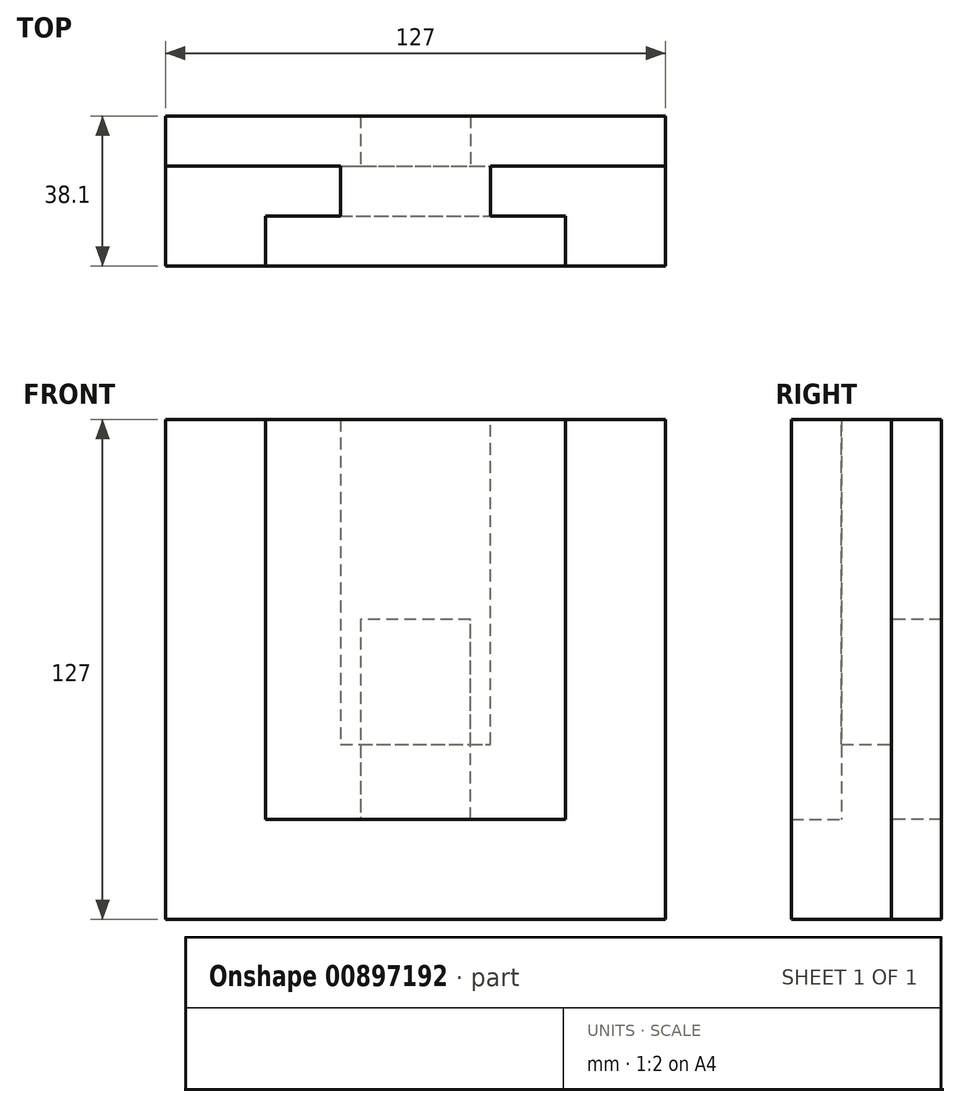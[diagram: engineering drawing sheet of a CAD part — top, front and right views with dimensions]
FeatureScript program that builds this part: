
annotation { "Feature Type Name" : "Feature", "Feature Type Description" : "" }
export const myFeature = defineFeature(function(context is Context, id is Id, definition is map)
    precondition{}
    {
        {
            var Q0;
            Q0=qCreatedBy(makeId("Front.planeOp"),FACE);
            var sketch = newSketch(context, id + "F0", { "sketchPlane" : qUnion([Q0])});
            skLineSegment(sketch, "E0.bottom", {"start": v(-63.5, 63.5) * mm, "end": v(63.5, 63.5) * mm});
            skLineSegment(sketch, "E0.top", {"start": v(-63.5, -63.5) * mm, "end": v(63.5, -63.5) * mm});
            skLineSegment(sketch, "E0.left", {"start": v(-63.5, 63.5) * mm, "end": v(-63.5, -63.5) * mm});
            skLineSegment(sketch, "E0.right", {"start": v(63.5, 63.5) * mm, "end": v(63.5, -63.5) * mm});
            skPoint(sketch, "E0.middle", {"position": v(0, 0) * mm});
            skLineSegment(sketch, "E1", {"start": v(-38.1, 63.5) * mm, "end": v(-38.1, -38.1) * mm});
            skLineSegment(sketch, "E2", {"start": v(-38.1, -38.1) * mm, "end": v(38.1, -38.1) * mm});
            skLineSegment(sketch, "E3", {"start": v(38.1, -38.1) * mm, "end": v(38.1, 63.5) * mm});
            skLineSegment(sketch, "E4", {"start": v(-19.05, 63.5) * mm, "end": v(-19.05, -19.05) * mm});
            skLineSegment(sketch, "E5", {"start": v(-19.05, -19.05) * mm, "end": v(19.05, -19.05) * mm});
            skLineSegment(sketch, "E6", {"start": v(19.05, -19.05) * mm, "end": v(19.05, 63.5) * mm});
            skLineSegment(sketch, "E7", {"start": v(13.97, -19.05) * mm, "end": v(13.97, 12.7) * mm});
            skLineSegment(sketch, "E8", {"start": v(13.97, 12.7) * mm, "end": v(-13.97, 12.7) * mm});
            skLineSegment(sketch, "E9", {"start": v(-13.97, 12.7) * mm, "end": v(-13.97, -19.05) * mm});
            skLineSegment(sketch, "E10", {"start": v(0, 130.1) * mm, "end": v(0, 0) * mm, "construction": true});
            skLineSegment(sketch, "E11", {"start": v(0, -117.96) * mm, "end": v(0, 0) * mm, "construction": true});
            skLineSegment(sketch, "E12", {"start": v(13.97, -19.05) * mm, "end": v(13.97, -38.1) * mm});
            skLineSegment(sketch, "E13", {"start": v(13.97, -38.1) * mm, "end": v(-13.97, -38.1) * mm});
            skLineSegment(sketch, "E14", {"start": v(-13.97, -38.1) * mm, "end": v(-13.97, -19.05) * mm});
            skSolve(sketch);
        }
        {
            var Q0;
            Q0=makeQuery(id+"F0.imprint","IMPRINT",FACE,{"disambiguationData":[TD([[makeQuery(id+"F0.imprint","IMPRINT",EDGE,{"derivedFrom":sQuery(id+"F0.wireOp",EDGE,"E0.top")}),1.0]])]});
            var Q1;
            Q1=sQuery(id+"F0.wireOp",EDGE,"E0.left");
            var Q2;
            Q2=sQuery(id+"F0.wireOp",EDGE,"E0.bottom");
            var Q3;
            Q3=sQuery(id+"F0.wireOp",EDGE,"E1");
            var Q4;
            Q4=sQuery(id+"F0.wireOp",EDGE,"E2");
            var Q5;
            Q5=sQuery(id+"F0.wireOp",EDGE,"E3");
            var Q6;
            Q6=sQuery(id+"F0.wireOp",EDGE,"E0.right");
            var Q7;
            Q7=sQuery(id+"F0.wireOp",EDGE,"E0.top");
            extrude(context, id + "F1", {"entities" : qUnion([Q0]), "surfaceEntities" : qUnion([Q1, Q2, Q3, Q4, Q5, Q6, Q7]), "depth" : 25.4 * mm, "offsetDistance" : 25.4 * mm});
        }
        {
            var Q0;
            {var subQ0=sQuery(id+"F0.wireOp",EDGE,"E1");Q0=makeQuery(id+"F0.imprint","IMPRINT",FACE,{"disambiguationData":[TD([[makeQuery(id+"F0.imprint","IMPRINT",EDGE,{"derivedFrom":subQ0}),1.0]])]});}
            var Q1;
            {var subQ0=sQuery(id+"F0.wireOp",EDGE,"E12");Q1=makeQuery(id+"F0.imprint","IMPRINT",FACE,{"disambiguationData":[TD([[makeQuery(id+"F0.imprint","IMPRINT",EDGE,{"derivedFrom":subQ0}),-1.0]])]});}
            var Q2;
            {var subQ0=sQuery(id+"F0.wireOp",EDGE,"E3");Q2=makeQuery(id+"F0.imprint","IMPRINT",FACE,{"disambiguationData":[TD([[makeQuery(id+"F0.imprint","IMPRINT",EDGE,{"derivedFrom":subQ0}),1.0]])]});}
            extrude(context, id + "F2", {"entities" : qUnion([Q0, Q1, Q2]), "operationType" : NewBodyOperationType.ADD, "depth" : 12.7 * mm, "offsetDistance" : 25.4 * mm});
        }
        {
            var Q0;
            {var subQ0=sQuery(id+"F0.wireOp",EDGE,"E7");Q0=makeQuery(id+"F0.imprint","IMPRINT",FACE,{"disambiguationData":[TD([[makeQuery(id+"F0.imprint","IMPRINT",EDGE,{"derivedFrom":subQ0}),1.0]])]});}
            var Q1;
            {var subQ0=sQuery(id+"F0.wireOp",EDGE,"E12");Q1=makeQuery(id+"F0.imprint","IMPRINT",FACE,{"disambiguationData":[TD([[makeQuery(id+"F0.imprint","IMPRINT",EDGE,{"derivedFrom":subQ0}),-1.0]])]});}
            extrude(context, id + "F3", {"entities" : qUnion([Q0, Q1]), "operationType" : NewBodyOperationType.ADD, "oppositeDirection" : true, "depth" : 12.7 * mm, "offsetDistance" : 25.4 * mm});
        }
        {
            var Q0;
            Q0=makeQuery(id+"F0.imprint","IMPRINT",FACE,{"disambiguationData":[TD([[makeQuery(id+"F0.imprint","IMPRINT",EDGE,{"derivedFrom":sQuery(id+"F0.wireOp",EDGE,"E0.top")}),1.0]])]});
            var Q1;
            {var subQ0=sQuery(id+"F0.wireOp",EDGE,"E3");Q1=makeQuery(id+"F0.imprint","IMPRINT",FACE,{"disambiguationData":[TD([[makeQuery(id+"F0.imprint","IMPRINT",EDGE,{"derivedFrom":subQ0}),1.0]])]});}
            var Q2;
            {var subQ3=sQuery(id+"F0.wireOp",EDGE,"E4");Q2=makeQuery(id+"F0.imprint","IMPRINT",FACE,{"disambiguationData":[TD([[makeQuery(id+"F0.imprint","IMPRINT",EDGE,{"derivedFrom":subQ3}),1.0]])]});}
            var Q3;
            {var subQ1=sQuery(id+"F0.wireOp",EDGE,"E1");Q3=makeQuery(id+"F0.imprint","IMPRINT",FACE,{"disambiguationData":[TD([[makeQuery(id+"F0.imprint","IMPRINT",EDGE,{"derivedFrom":subQ1}),1.0]])]});}
            var Q4;
            {var subQ0=sQuery(id+"F0.wireOp",EDGE,"E12");Q4=makeQuery(id+"F0.imprint","IMPRINT",FACE,{"disambiguationData":[TD([[makeQuery(id+"F0.imprint","IMPRINT",EDGE,{"derivedFrom":subQ0}),-1.0]])]});}
            var Q5;
            {var subQ0=sQuery(id+"F0.wireOp",EDGE,"E7");Q5=makeQuery(id+"F0.imprint","IMPRINT",FACE,{"disambiguationData":[TD([[makeQuery(id+"F0.imprint","IMPRINT",EDGE,{"derivedFrom":subQ0}),1.0]])]});}
            extrude(context, id + "F4", {"entities" : qUnion([Q0, Q1, Q2, Q3, Q4, Q5]), "depth" : 25.4 * mm, "offsetDistance" : 25.4 * mm, "hasSecondDirection" : true, "secondDirectionOppositeDirection" : true, "secondDirectionDepth" : 12.7 * mm});
        }
        {
            var Q0;
            Q0=makeQuery(id+"F1.opExtrude","SWEPT_BODY",BODY,{"disambiguationData":[OSD([sQuery(id+"F0.wireOp",EDGE,"E0.bottom"),sQuery(id+"F0.wireOp",EDGE,"E0.top"),sQuery(id+"F0.wireOp",EDGE,"E0.left"),sQuery(id+"F0.wireOp",EDGE,"E0.right"),sQuery(id+"F0.wireOp",EDGE,"E1"),sQuery(id+"F0.wireOp",EDGE,"E2"),sQuery(id+"F0.wireOp",EDGE,"E3"),sQuery(id+"F0.wireOp",EDGE,"E13")])]});
            var Q1;
            Q1=makeQuery(id+"F4.opExtrude","SWEPT_BODY",BODY,{"disambiguationData":[OSD([sQuery(id+"F0.wireOp",EDGE,"E0.bottom"),sQuery(id+"F0.wireOp",EDGE,"E0.top"),sQuery(id+"F0.wireOp",EDGE,"E0.left"),sQuery(id+"F0.wireOp",EDGE,"E0.right")])]});
            booleanBodies(context, id + "F5", {"operationType" : BooleanOperationType.INTERSECTION, "tools" : qUnion([Q0, Q1]), "keepTools" : true});
        }
    });
